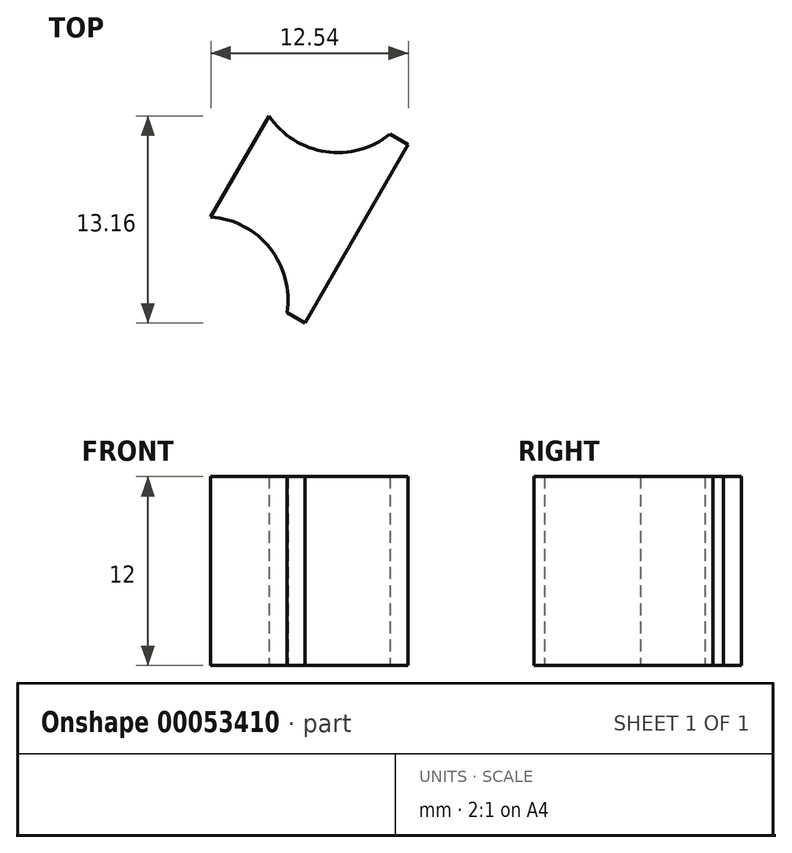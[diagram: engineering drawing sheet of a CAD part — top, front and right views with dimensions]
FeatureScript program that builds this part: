
annotation { "Feature Type Name" : "Feature", "Feature Type Description" : "" }
export const myFeature = defineFeature(function(context is Context, id is Id, definition is map)
    precondition{}
    {
        {
            var Q0;
            Q0=qCreatedBy(makeId("Top.planeOp"),FACE);
            var sketch = newSketch(context, id + "F0", { "sketchPlane" : qUnion([Q0])});
            skCircle(sketch, "E0", {"center": v(-23, 23) * mm, "radius": 5.25 * mm});
            skLineSegment(sketch, "E1", {"start": v(0, 0) * mm, "end": v(0, 33.45) * mm, "construction": true});
            skCircle(sketch, "E2.MirrorC", {"center": v(23, 23) * mm, "radius": 5.25 * mm});
            skCircle(sketch, "E3.1.0", {"center": v(-8.42, -31.42) * mm, "radius": 5.25 * mm});
            skCircle(sketch, "E3.1.1", {"center": v(-31.42, 8.42) * mm, "radius": 5.25 * mm});
            skCircle(sketch, "E3.2.0", {"center": v(31.42, 8.42) * mm, "radius": 5.25 * mm});
            skCircle(sketch, "E3.2.1", {"center": v(8.42, -31.42) * mm, "radius": 5.25 * mm});
            skPoint(sketch, "E3.center", {"position": v(0, 0) * mm});
            skLineSegment(sketch, "E4", {"start": v(0, 0) * mm, "end": v(-35.85, 20.7) * mm, "construction": true});
            skLineSegment(sketch, "E5", {"start": v(-31.07, 13.66) * mm, "end": v(-27.36, 20.08) * mm});
            skLineSegment(sketch, "E6", {"start": v(-26.23, 7.59) * mm, "end": v(-19.69, 18.93) * mm, "construction": true});
            skLineSegment(sketch, "E7", {"start": v(-26.23, 7.59) * mm, "end": v(-25.08, 6.92) * mm});
            skLineSegment(sketch, "E8", {"start": v(-25.08, 6.92) * mm, "end": v(-18.53, 18.26) * mm});
            skLineSegment(sketch, "E9", {"start": v(-18.53, 18.26) * mm, "end": v(-19.69, 18.93) * mm});
            skSolve(sketch);
        }
        {
            var Q0;
            {var subQ1=sQuery(id+"F0.wireOp",EDGE,"E5");Q0=makeQuery(id+"F0.imprint","IMPRINT",FACE,{"disambiguationData":[TD([[makeQuery(id+"F0.imprint","IMPRINT",EDGE,{"derivedFrom":subQ1}),-1.0]])]});}
            extrude(context, id + "F1", {"entities" : qUnion([Q0]), "depth" : 12 * mm});
        }
    });
